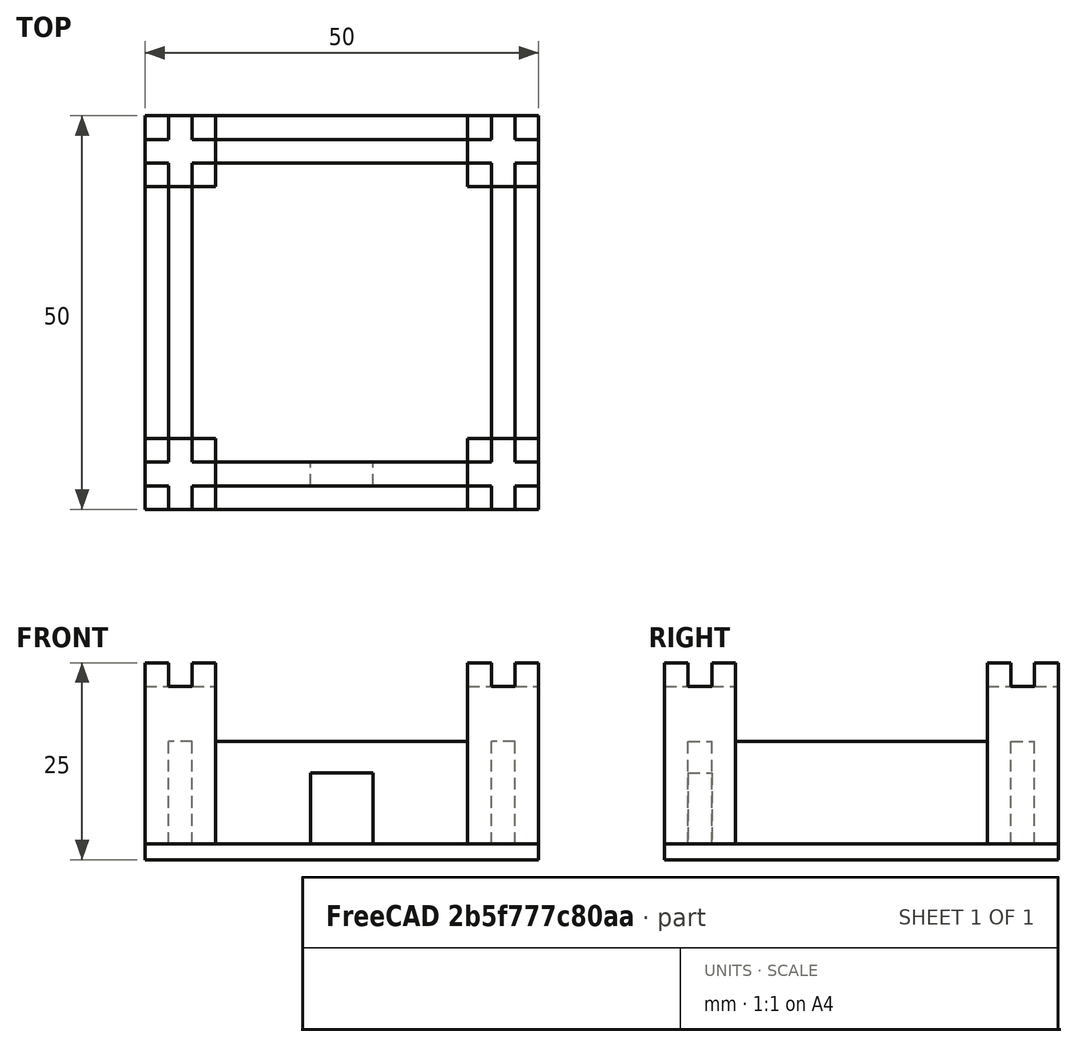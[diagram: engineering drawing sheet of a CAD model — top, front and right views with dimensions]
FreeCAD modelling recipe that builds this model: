
FCSTD DOCUMENT  (FreeCAD 0.17R13217 (Git))
Label: 08-castillo
License: All rights reserved
LicenseURL: http://en.wikipedia.org/wiki/All_rights_reserved
objects: Part::Box×11, Part::MultiFuse×5, Part::Cut×1
note: 17 computed .brp shape members not serialized (recipe doc carries the construction recipe); baked Part::Feature solids carry a one-line shape summary decoded from their .brp

FEATURE [Part::Box] Box  label="base"
  AttacherType = Attacher::AttachEngine3D
  Height = 2
  Length = 50
  Placement = pos=(0,0,-2) rot=(0,0,1;0rad)
  Width = 50
FEATURE [Part::Box] Box001  label="Almena"
  AttacherType = Attacher::AttachEngine3D
  Height = 3
  Length = 3
  Placement = pos=(0,0,20) rot=(0,0,1;0rad)
  Width = 3
FEATURE [Part::Box] Box002  label="Base-torre"
  AttacherType = Attacher::AttachEngine3D
  Height = 20
  Length = 9
  Width = 9
FEATURE [Part::Box] Box003  label="Almena001"
  AttacherType = Attacher::AttachEngine3D
  Height = 3
  Length = 3
  Placement = pos=(6,0,20) rot=(0,0,1;0rad)
  Width = 3
FEATURE [Part::Box] Box004  label="Almena002"
  AttacherType = Attacher::AttachEngine3D
  Height = 3
  Length = 3
  Placement = pos=(0,6,20) rot=(0,0,1;0rad)
  Width = 3
FEATURE [Part::Box] Box005  label="Almena003"
  AttacherType = Attacher::AttachEngine3D
  Height = 3
  Length = 3
  Placement = pos=(6,6,20) rot=(0,0,1;0rad)
  Width = 3
FEATURE [Part::MultiFuse] Fusion  label="Torre-1"
  Refine = true
  Shapes = -> [Box001,Box005,Box004,Box003,Box002]
FEATURE [Part::MultiFuse] Fusion001  label="Torre-002"
  Placement = pos=(41,0,0) rot=(0,0,1;0rad)
  Refine = true
  Shapes = -> [Box001,Box005,Box004,Box003,Box002]
FEATURE [Part::MultiFuse] Fusion002  label="Torre-003"
  Placement = pos=(0,41,0) rot=(0,0,1;0rad)
  Refine = true
  Shapes = -> [Box001,Box005,Box004,Box003,Box002]
FEATURE [Part::MultiFuse] Fusion003  label="Torre-004"
  Placement = pos=(41,41,0) rot=(0,0,1;0rad)
  Refine = true
  Shapes = -> [Box001,Box005,Box004,Box003,Box002]
FEATURE [Part::Box] Box006  label="Muro"
  AttacherType = Attacher::AttachEngine3D
  Height = 13
  Length = 32
  Placement = pos=(9,3,0) rot=(0,0,1;0rad)
  Width = 3
FEATURE [Part::Box] Box007  label="Muro001"
  AttacherType = Attacher::AttachEngine3D
  Height = 13
  Length = 32
  Placement = pos=(9,44,0) rot=(0,0,1;0rad)
  Width = 3
FEATURE [Part::Box] Box008  label="Muro002"
  AttacherType = Attacher::AttachEngine3D
  Height = 13
  Length = 32
  Placement = pos=(6,9,0) rot=(0,0,1;1.5708rad)
  Width = 3
FEATURE [Part::Box] Box009  label="Muro003"
  AttacherType = Attacher::AttachEngine3D
  Height = 13
  Length = 32
  Placement = pos=(47,9,0) rot=(0,0,1;1.5708rad)
  Width = 3
FEATURE [Part::Box] Box010  label="puerta"
  AttacherType = Attacher::AttachEngine3D
  Height = 9
  Length = 8
  Placement = pos=(21,0,0) rot=(0,0,1;0rad)
  Width = 10
FEATURE [Part::Cut] Cut  label="Muro-puerta"
  Base = -> Box006
  Refine = true
  Tool = -> Box010
FEATURE [Part::MultiFuse] Fusion004  label="Castillo"
  Refine = true
  Shapes = -> [Fusion,Cut,Box009,Box007,Fusion002,Fusion001,Fusion003,Box008]
